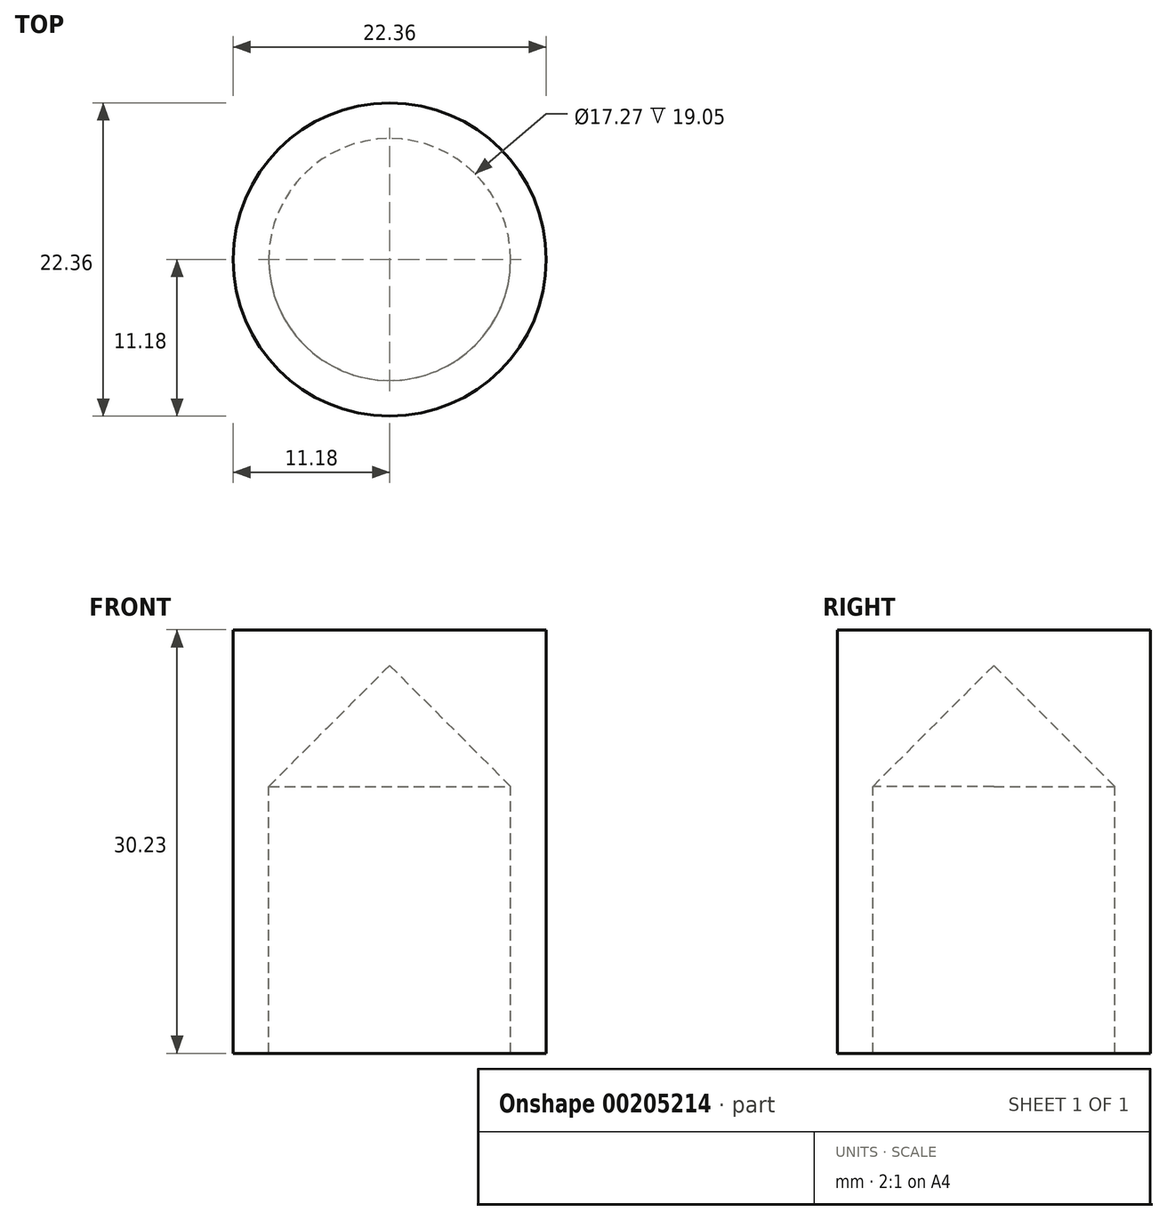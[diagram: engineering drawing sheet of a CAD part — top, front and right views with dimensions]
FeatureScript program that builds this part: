
annotation { "Feature Type Name" : "Feature", "Feature Type Description" : "" }
export const myFeature = defineFeature(function(context is Context, id is Id, definition is map)
    precondition{}
    {
        {
            var Q0;
            Q0=qCreatedBy(makeId("Front.planeOp"),FACE);
            var sketch = newSketch(context, id + "F0", { "sketchPlane" : qUnion([Q0])});
            skLineSegment(sketch, "E0", {"start": v(0, 30.23) * mm, "end": v(11.18, 30.23) * mm});
            skLineSegment(sketch, "E1", {"start": v(11.18, 30.23) * mm, "end": v(11.18, 0) * mm});
            skLineSegment(sketch, "E2", {"start": v(11.18, 0) * mm, "end": v(8.64, 0) * mm});
            skLineSegment(sketch, "E3", {"start": v(8.64, 0) * mm, "end": v(8.64, 19.05) * mm});
            skLineSegment(sketch, "E4", {"start": v(8.64, 19.05) * mm, "end": v(0, 27.69) * mm});
            skLineSegment(sketch, "E5", {"start": v(0, 27.69) * mm, "end": v(0, 30.23) * mm});
            skLineSegment(sketch, "E6", {"start": v(0, 27.69) * mm, "end": v(0, 0) * mm, "construction": true});
            skLineSegment(sketch, "E7", {"start": v(-8.64, 0) * mm, "end": v(8.64, 0) * mm, "construction": true});
            skSolve(sketch);
        }
        {
            var Q0;
            Q0 = qSketchRegion(id + "F0", true);
            var Q1;
            Q1=sQuery(id+"F0.wireOp",EDGE,"E6");
            revolve(context, id + "F1", {"entities" : qUnion([Q0]), "axis" : qUnion([Q1]), "revolveType" : RevolveType.FULL});
        }
    });
